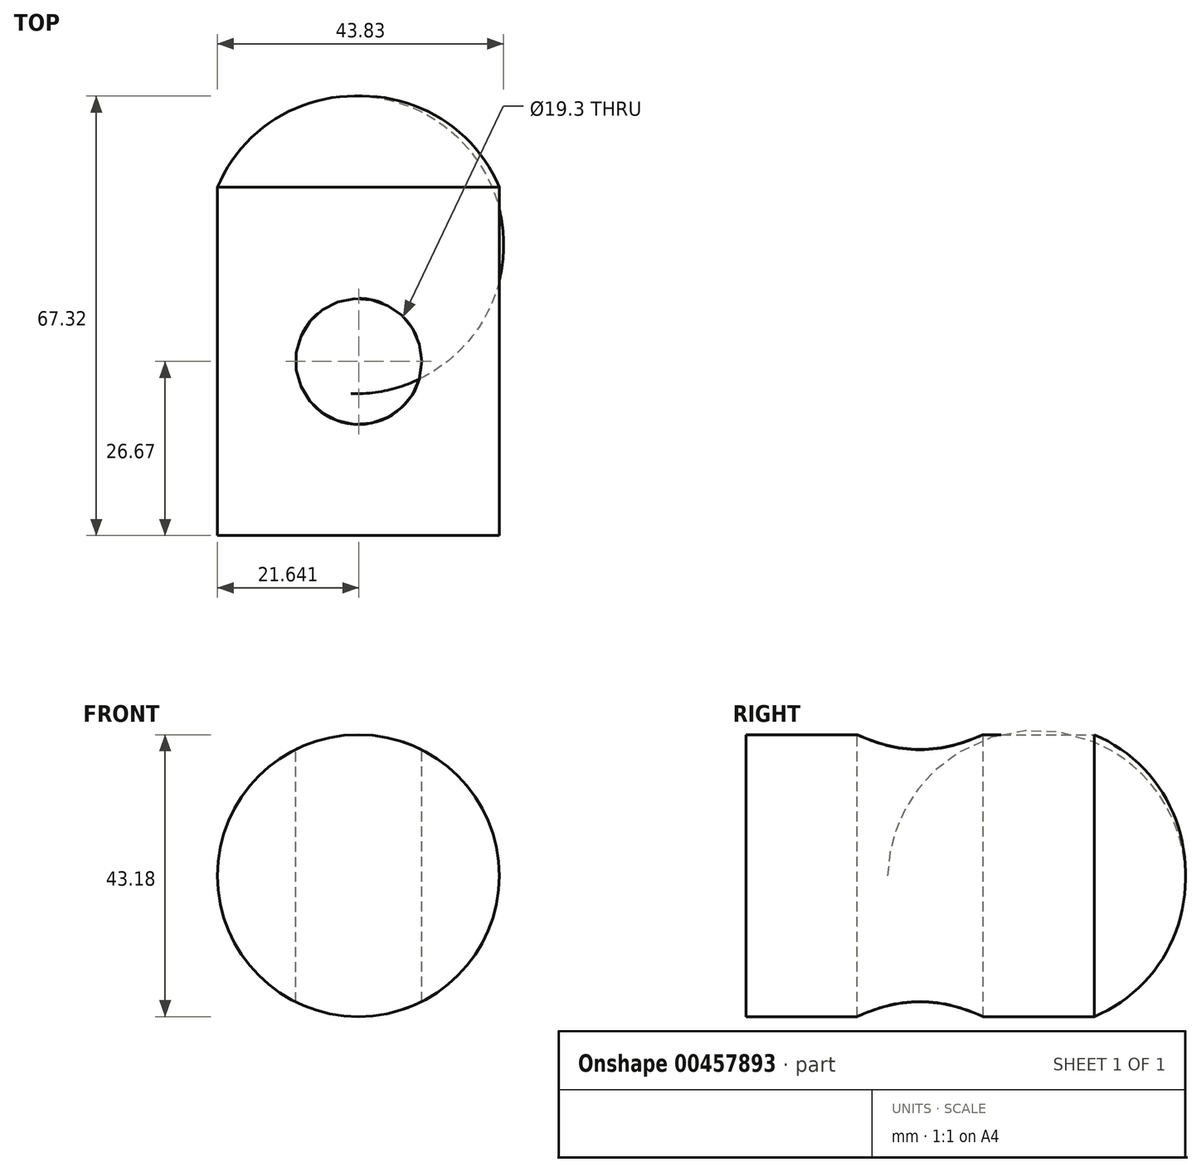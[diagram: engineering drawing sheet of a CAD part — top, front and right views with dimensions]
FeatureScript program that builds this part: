
annotation { "Feature Type Name" : "Feature", "Feature Type Description" : "" }
export const myFeature = defineFeature(function(context is Context, id is Id, definition is map)
    precondition{}
    {
        {
            var Q0;
            Q0=qCreatedBy(makeId("Top.planeOp"),FACE);
            var sketch = newSketch(context, id + "F0", { "sketchPlane" : qUnion([Q0])});
            skLineSegment(sketch, "E0.top", {"start": v(-82.27, 0) * mm, "end": v(-60.68, 0) * mm});
            skLineSegment(sketch, "E0.left", {"start": v(-82.27, 53.34) * mm, "end": v(-82.27, 0) * mm});
            skArc(sketch, "E1", {"start": v(-60.68, 67.31) * mm, "mid": v(-73.63, 63.66) * mm, "end": v(-82.27, 53.34) * mm});
            skLineSegment(sketch, "E2", {"start": v(-60.68, 67.31) * mm, "end": v(-60.68, 0) * mm});
            skPoint(sketch, "E3.orphan", {"position": v(-39.1, 0) * mm});
            skSolve(sketch);
        }
        {
            var Q0;
            Q0 = qSketchRegion(id + "F0", true);
            var Q1;
            Q1=sQuery(id+"F0.wireOp",EDGE,"E2");
            revolve(context, id + "F1", {"entities" : qUnion([Q0]), "axis" : qUnion([Q1]), "revolveType" : RevolveType.FULL});
        }
        {
            var Q0;
            Q0=qCreatedBy(makeId("Top.planeOp"),FACE);
            var sketch = newSketch(context, id + "F2", { "sketchPlane" : qUnion([Q0])});
            skLineSegment(sketch, "E4", {"start": v(-82.5, 53.34) * mm, "end": v(-38.76, 53.34) * mm, "construction": true});
            skLineSegment(sketch, "E5", {"start": v(-60.63, 53.34) * mm, "end": v(-60.63, 0) * mm, "construction": true});
            skCircle(sketch, "E6", {"center": v(-60.63, 26.67) * mm, "radius": 9.65 * mm});
            skSolve(sketch);
        }
        {
            var Q0;
            Q0 = qSketchRegion(id + "F2", true);
            extrude(context, id + "F3", {"entities" : qUnion([Q0]), "operationType" : NewBodyOperationType.REMOVE, "endBound" : BoundingType.SYMMETRIC, "oppositeDirection" : true, "depth" : 50.8 * mm});
        }
    });
